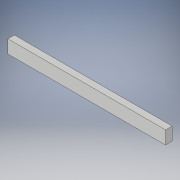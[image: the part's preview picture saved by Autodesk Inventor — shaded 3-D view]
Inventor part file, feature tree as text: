
AUTODESK INVENTOR PART (.ipt)
format: ipt  version: 2017 (Build 210142000, 142)  size: 92,160 bytes
history: native  units: in
note: dims shown in document units (in); Inventor stores cm internally (conversion verified against a paired STEP export)
features: extrude x1, sketch x1
ambient origin geometry x8: Origin, YZ Plane, XZ Plane, XY Plane, X Axis, Y Axis, Z Axis, Center Point
bodies: Solid1 (feature_tree)
feature tree (2):
  extrude  "Extrusion1"  Depth=3.0in
  sketch  "Sketch1"  dims[d0=72.0in d1=3.0in d2=6.0in d3=0.0in]
